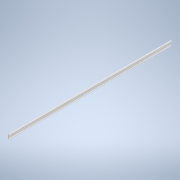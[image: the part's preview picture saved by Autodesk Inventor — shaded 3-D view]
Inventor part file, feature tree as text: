
AUTODESK INVENTOR PART (.ipt)
format: ipt  version: 2020 (Build 240168000, 168)  size: 112,640 bytes
history: native  units: mm
features: extrude x1, sketch x1
ambient origin geometry x8: Origin, YZ Plane, XZ Plane, XY Plane, X Axis, Y Axis, Z Axis, Center Point
bodies: Solid1 (feature_tree)
feature tree (2):
  extrude  "Extrusion1"  Depth=150.0mm
  sketch  "Sketch1"  dims[d0=43.0mm d1=150.0mm d2=15.0mm d3=15.0mm d4=3.0mm d5=5740.0mm d6=0.0mm]
